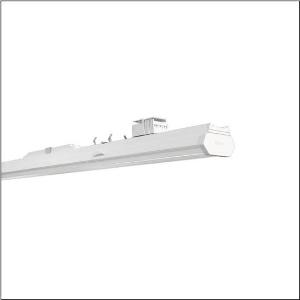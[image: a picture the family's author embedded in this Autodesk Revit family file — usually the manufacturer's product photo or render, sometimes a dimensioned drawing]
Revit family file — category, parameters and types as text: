
# Revit family: licross_r__21_protected_ho_52td12dn4e5m3c_ce33
name_source: partatom
category: Lighting Fixtures
units: mm (PartAtom-declared; Revit-internal decimal feet)

## family parameters
Cut with Voids When Loaded = No
Host = Face
Light Source = No
Part Type = Normal
Room Calculation Point = No
Round Connector Dimension = Use Diameter
Shared = No

## types (1)
- --- (1 x LED, 910 lm, 7.6 W, 4000K)
    Apparent Load = 8 VA
    CIE Flux Codes = 70 91 97 98 100
    Color Rendering = 80
    Color Temperature = 4000K
    Default Elevation = 1800 mm
    Description = Licross® 21 Protected HO, luminaire insert, of sheet steel, galvanised, coil coated, white, length: 1.500mm, width: 90mm, height: 103mm, LED rated luminous flux: 14.690lm, light colour: 840, control gear: DALI 2, with plug, 6-pole, with phase selection, for trunking rail, 14-core, mains connection: 220..240V, AC, 50/60Hz, rated input power: 89W, for trunking rail, 14-core, halogen-free wiring, for emergency light function, converter,control gear: single battery element, battery: LiFeP04, 9Ah, primary light control with lens, of plastic, primary optical cover: cover, of PMMA, light emission: direct distribution, primary light characteristic: symmetric, protection rating (complete): IP54, insulation class (complete): insulation class I (protective earthing), certification: CE, UKCA, protection symbol: D if used in an environment with non-conductive dust loads with corresponding accessories, impact resistance: IK06, permissible ambient temperature for indoor applications: +5..+30°C, standard: EN 60598-2-22, LABS conformity tested according to VDMA 24364:2018-05, reducing of maximum allowable ambient temperature of 5°C with ceiling mounting, corresponds to IFS (International Featured Standards) requirements for safety and quality in the food industry, packaging unit: 1 piece
    Height = 92 mm
    Lamp = 1 x LED
    Lamp Light Flux = 910 lm
    Lamp Power = 7.6 W
    Lamp count = 1
    Length = 1500 mm
    Luminous efficacy = 120 lm/W
    Manufacturer = Siteco
    ModVariant = No
    Model = 52TD12DN4E5M3C
    Mounting Place = Ceiling
    Mounting Type = Pendant
    Number of Poles = 1
    OnlyDefault = Yes
    Power Factor = 1
    Product Name = Licross® 21 Protected HO
    Product group = luminaire insert
    ProductGroupID = 901
    Protection Class = Protection class I
    Protection Degree = IP 54
    RLX_Detail_Level = 1
    RLX_Emergency_Light_Flux = 0 lm
    RLX_Emergency_Type = 0
    RLX_Emergency_Type_DB = No
    RlxData = <blob elided: 24869 chars, md5=1ea6d132>
    Socket = socket
    Standby Power = 0 W
    System Light Flux = 910 lm
    System Power = 8 W
    Type Comments = : emergency light operation: 3 h
    Type Image = l_1256148.jpg
    URL = http://relux.com
    VarID = @adj_059469
    Voltage = 0 V
    Weight = 0.00 kg
    Width = 88 mm

## geometry (parser evidence)
native form markers: Blend x4, Sweep x10
no freeform markers — native parametric forms only
